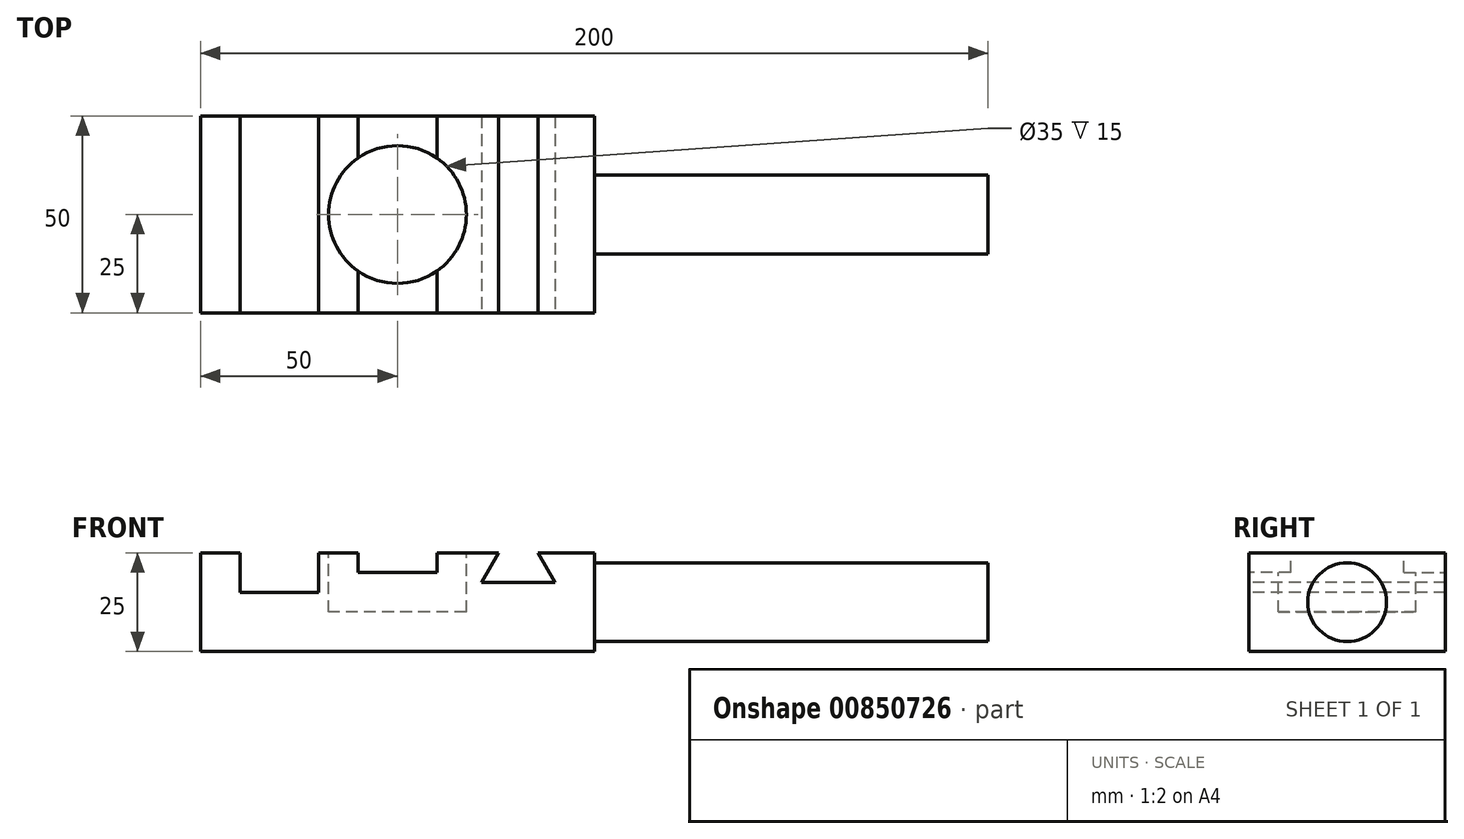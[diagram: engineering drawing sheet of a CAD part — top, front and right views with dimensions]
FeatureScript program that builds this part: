
annotation { "Feature Type Name" : "Feature", "Feature Type Description" : "" }
export const myFeature = defineFeature(function(context is Context, id is Id, definition is map)
    precondition{}
    {
        {
            var Q0;
            Q0=qCreatedBy(makeId("Top.planeOp"),FACE);
            var sketch = newSketch(context, id + "F0", { "sketchPlane" : qUnion([Q0])});
            skLineSegment(sketch, "E0.bottom", {"start": v(-50, 25) * mm, "end": v(50, 25) * mm});
            skLineSegment(sketch, "E0.top", {"start": v(-50, -25) * mm, "end": v(50, -25) * mm});
            skLineSegment(sketch, "E0.left", {"start": v(-50, 25) * mm, "end": v(-50, -25) * mm});
            skLineSegment(sketch, "E0.right", {"start": v(50, 25) * mm, "end": v(50, -25) * mm});
            skPoint(sketch, "E0.middle", {"position": v(0, 0) * mm});
            skSolve(sketch);
        }
        {
            var Q0;
            Q0=makeQuery(id+"F0.imprint","IMPRINT",FACE,{"disambiguationData":[TD([[makeQuery(id+"F0.imprint","IMPRINT",EDGE,{"derivedFrom":sQuery(id+"F0.wireOp",EDGE,"E0.bottom")}),-1.0]])]});
            extrude(context, id + "F1", {"entities" : qUnion([Q0]), "depth" : 25 * mm, "offsetDistance" : 25 * mm});
        }
        {
            var Q0;
            Q0=makeQuery(id+"F1.opExtrude","CAP_FACE",FACE,{"disambiguationData":[OSD([sQuery(id+"F0.wireOp",EDGE,"E0.bottom"),sQuery(id+"F0.wireOp",EDGE,"E0.top"),sQuery(id+"F0.wireOp",EDGE,"E0.left"),sQuery(id+"F0.wireOp",EDGE,"E0.right")])],"isStart":false});
            var sketch = newSketch(context, id + "F2", { "sketchPlane" : qUnion([Q0])});
            skLineSegment(sketch, "E1.bottom", {"start": v(-40, 25) * mm, "end": v(-20, 25) * mm});
            skLineSegment(sketch, "E1.top", {"start": v(-40, -25) * mm, "end": v(-20, -25) * mm});
            skLineSegment(sketch, "E1.left", {"start": v(-40, 25) * mm, "end": v(-40, -25) * mm});
            skLineSegment(sketch, "E1.right", {"start": v(-20, 25) * mm, "end": v(-20, -25) * mm});
            skLineSegment(sketch, "E2", {"start": v(-10, 25) * mm, "end": v(-10, -25) * mm});
            skLineSegment(sketch, "E3", {"start": v(-10, -25) * mm, "end": v(10, -25) * mm});
            skLineSegment(sketch, "E4", {"start": v(10, -25) * mm, "end": v(10, 25) * mm});
            skLineSegment(sketch, "E5", {"start": v(10, 25) * mm, "end": v(-10, 25) * mm});
            skPoint(sketch, "E6", {"position": v(0, -25) * mm});
            skPoint(sketch, "E7", {"position": v(0, 25) * mm});
            skLineSegment(sketch, "E8", {"start": v(0, 25) * mm, "end": v(0, -25) * mm, "construction": true});
            skPoint(sketch, "E9", {"position": v(0, 0) * mm});
            skSolve(sketch);
        }
        {
            var Q0;
            Q0=makeQuery(id+"F2.imprint","IMPRINT",FACE,{"disambiguationData":[TD([[makeQuery(id+"F2.imprint","IMPRINT",EDGE,{"derivedFrom":sQuery(id+"F2.wireOp",EDGE,"E1.bottom")}),-1.0]])]});
            extrude(context, id + "F3", {"entities" : qUnion([Q0]), "operationType" : NewBodyOperationType.REMOVE, "oppositeDirection" : true, "depth" : 10 * mm, "offsetDistance" : 25 * mm});
        }
        {
            var Q0;
            Q0=makeQuery(id+"F2.imprint","IMPRINT",FACE,{"disambiguationData":[TD([[makeQuery(id+"F2.imprint","IMPRINT",EDGE,{"derivedFrom":sQuery(id+"F2.wireOp",EDGE,"E2")}),1.0]])]});
            extrude(context, id + "F4", {"entities" : qUnion([Q0]), "operationType" : NewBodyOperationType.REMOVE, "oppositeDirection" : true, "depth" : 5 * mm, "offsetDistance" : 25 * mm});
        }
        {
            var Q0;
            Q0=makeQuery(id+"F1.opExtrude","SWEPT_FACE",FACE,{"disambiguationData":[OSD([sQuery(id+"F0.wireOp",EDGE,"E0.top")])]});
            var sketch = newSketch(context, id + "F5", { "sketchPlane" : qUnion([Q0])});
            skLineSegment(sketch, "E10", {"start": v(25.67, 25) * mm, "end": v(21.34, 17.5) * mm});
            skLineSegment(sketch, "E11", {"start": v(21.34, 17.5) * mm, "end": v(40, 17.5) * mm});
            skLineSegment(sketch, "E12", {"start": v(40, 17.5) * mm, "end": v(35.67, 25) * mm});
            skLineSegment(sketch, "E13", {"start": v(35.67, 25) * mm, "end": v(25.67, 25) * mm});
            skSolve(sketch);
        }
        {
            var Q0;
            Q0=makeQuery(id+"F5.imprint","IMPRINT",FACE,{"disambiguationData":[TD([[makeQuery(id+"F5.imprint","IMPRINT",EDGE,{"derivedFrom":sQuery(id+"F5.wireOp",EDGE,"E10")}),1.0]])]});
            var Q1;
            Q1=makeQuery(id+"F1.opExtrude","SWEPT_FACE",FACE,{"disambiguationData":[OSD([sQuery(id+"F0.wireOp",EDGE,"E0.bottom")])]});
            extrude(context, id + "F6", {"entities" : qUnion([Q0]), "operationType" : NewBodyOperationType.REMOVE, "endBound" : BoundingType.UP_TO_SURFACE, "oppositeDirection" : true, "depth" : 25 * mm, "endBoundEntityFace" : qUnion([Q1]), "offsetDistance" : 25 * mm});
        }
        {
            var Q0;
            Q0=makeQuery(id+"F1.opExtrude","SWEPT_FACE",FACE,{"disambiguationData":[OSD([sQuery(id+"F0.wireOp",EDGE,"E0.right")])]});
            var sketch = newSketch(context, id + "F7", { "sketchPlane" : qUnion([Q0])});
            skLineSegment(sketch, "E14", {"start": v(0, 25) * mm, "end": v(0, 0) * mm, "construction": true});
            skLineSegment(sketch, "E15", {"start": v(-25, 12.5) * mm, "end": v(25, 12.5) * mm, "construction": true});
            skCircle(sketch, "E16", {"center": v(0, 12.5) * mm, "radius": 10 * mm});
            skSolve(sketch);
        }
        {
            var Q0;
            Q0=makeQuery(id+"F7.imprint","IMPRINT",FACE,{"disambiguationData":[TD([[makeQuery(id+"F7.imprint","IMPRINT",EDGE,{"derivedFrom":sQuery(id+"F7.wireOp",EDGE,"E16")}),1.0]])]});
            extrude(context, id + "F8", {"entities" : qUnion([Q0]), "operationType" : NewBodyOperationType.ADD, "depth" : 100 * mm, "offsetDistance" : 25 * mm});
        }
        {
            var Q0;
            {var subQ0=sQuery(id+"F0.wireOp",EDGE,"E0.bottom");var subQ2=sQuery(id+"F0.wireOp",EDGE,"E0.top");var subQ4=makeQuery(id+"F3.opExtrude","SWEPT_FACE",FACE,{"disambiguationData":[OSD([sQuery(id+"F2.wireOp",EDGE,"E1.right")])]});var subQ5=sQuery(id+"F0.wireOp",EDGE,"E0.right");Q0=makeQuery(id+"F4.boolean.opBoolean","SPLIT",FACE,{"disambiguationData":[TD([makeQuery(id+"F3.boolean.opBoolean","COPY",FACE,{"derivedFrom":subQ4})])],"derivedFrom":makeQuery(id+"F3.boolean.opBoolean","SPLIT",FACE,{"disambiguationData":[TD([makeQuery(id+"F1.opExtrude","SWEPT_FACE",FACE,{"disambiguationData":[OSD([subQ5])]})])],"derivedFrom":makeQuery(id+"F1.opExtrude","CAP_FACE",FACE,{"disambiguationData":[OSD([subQ0,subQ2,sQuery(id+"F0.wireOp",EDGE,"E0.left"),subQ5])],"isStart":false})})});}
            var sketch = newSketch(context, id + "F9", { "sketchPlane" : qUnion([Q0])});
            skCircle(sketch, "E17", {"center": v(0, 0) * mm, "radius": 17.5 * mm});
            skSolve(sketch);
        }
        {
            var Q0;
            {var subQ0=sQuery(id+"F9.wireOp",EDGE,"E17");var subQ1=makeQuery(id+"F9.imprint","INTERSECT",VERTEX,{"derivedFrom":[makeQuery(id+"F3.boolean.opBoolean","COPY",EDGE,{"derivedFrom":makeQuery(id+"F3.opExtrude","CAP_EDGE",EDGE,{"disambiguationData":[OSD([sQuery(id+"F2.wireOp",EDGE,"E1.right")])],"isStart":true})}),subQ0]});Q0=makeQuery(id+"F9.imprint","IMPRINT",FACE,{"disambiguationData":[TD([[makeQuery(id+"F9.imprint","IMPRINT",EDGE,{"disambiguationData":[TD([[subQ1,1.0]])],"derivedFrom":subQ0}),1.0]])]});}
            var Q1;
            {var subQ0=sQuery(id+"F9.wireOp",EDGE,"E17");var subQ1=makeQuery(id+"F4.boolean.opBoolean","COPY",EDGE,{"derivedFrom":makeQuery(id+"F4.opExtrude","CAP_EDGE",EDGE,{"disambiguationData":[OSD([sQuery(id+"F2.wireOp",EDGE,"E2")])],"isStart":true})});var subQ2=makeQuery(id+"F9.imprint","INTERSECT",VERTEX,{"disambiguationData":[OD(0.0)],"derivedFrom":[subQ1,subQ0]});Q1=makeQuery(id+"F9.imprint","IMPRINT",FACE,{"disambiguationData":[TD([[makeQuery(id+"F9.imprint","IMPRINT",EDGE,{"disambiguationData":[TD([[subQ2,1.0]])],"derivedFrom":subQ0}),1.0]])]});}
            extrude(context, id + "F10", {"entities" : qUnion([Q0, Q1]), "operationType" : NewBodyOperationType.REMOVE, "oppositeDirection" : true, "depth" : 15 * mm, "offsetDistance" : 25 * mm});
        }
    });
